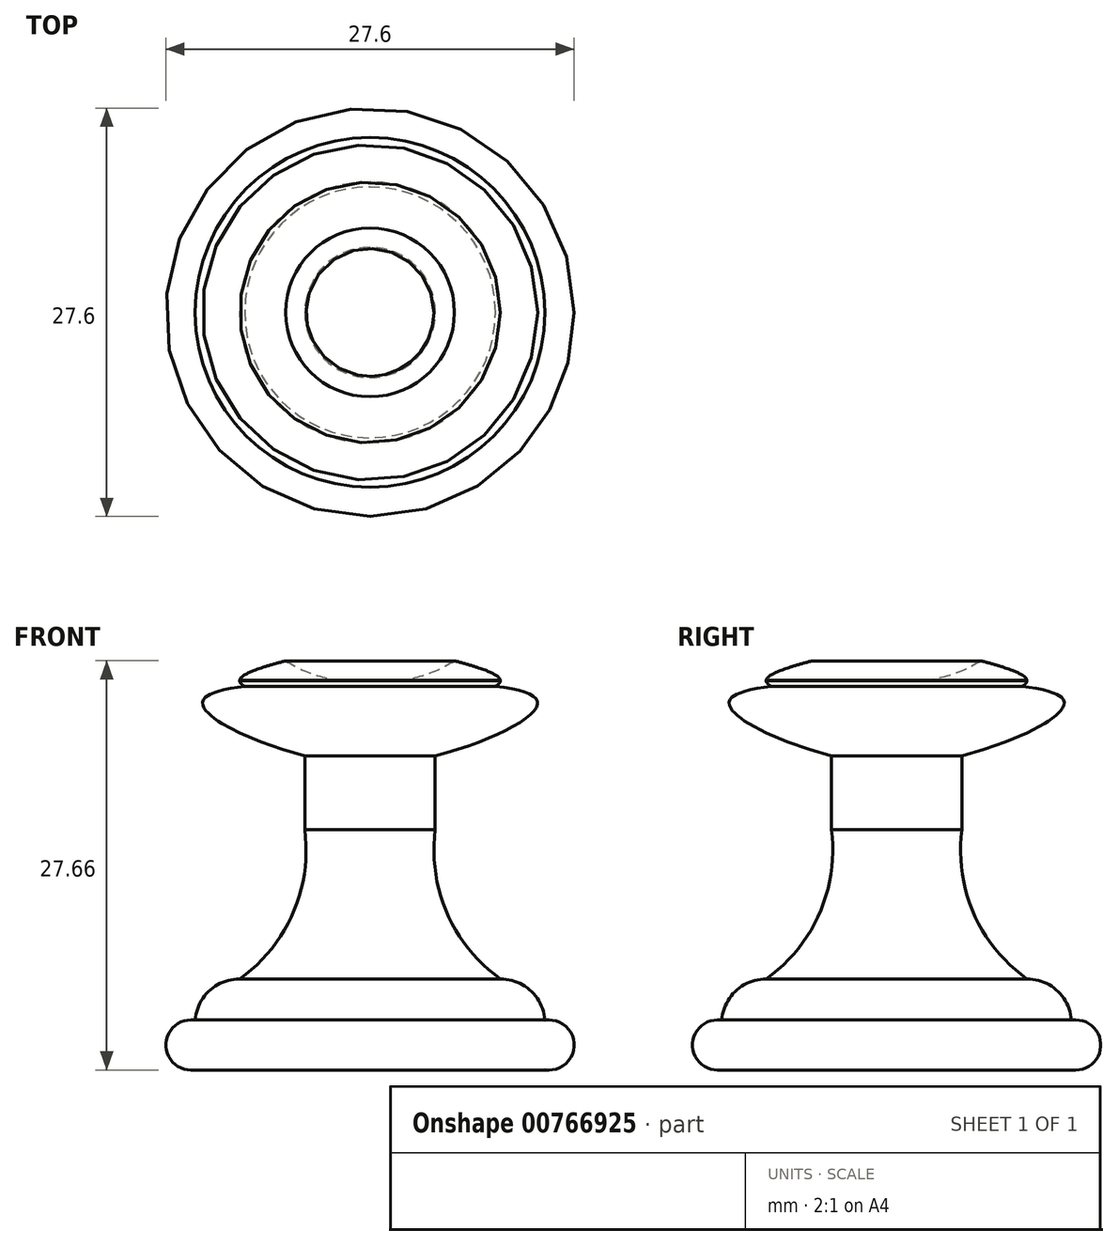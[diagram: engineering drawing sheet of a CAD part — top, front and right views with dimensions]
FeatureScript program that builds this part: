
annotation { "Feature Type Name" : "Feature", "Feature Type Description" : "" }
export const myFeature = defineFeature(function(context is Context, id is Id, definition is map)
    precondition{}
    {
        {
            var Q0;
            Q0=qCreatedBy(makeId("Front.planeOp"),FACE);
            var sketch = newSketch(context, id + "F0", { "sketchPlane" : qUnion([Q0])});
            skLineSegment(sketch, "E0.left", {"start": v(0, 2.22) * mm, "end": v(0, 4.66) * mm});
            skLineSegment(sketch, "E1", {"start": v(0, 4.66) * mm, "end": v(0, 8.36) * mm});
            skLineSegment(sketch, "E2", {"start": v(8.81, 8.36) * mm, "end": v(0, 8.36) * mm});
            skLineSegment(sketch, "E3", {"start": v(0, 8.36) * mm, "end": v(0, 28.5) * mm});
            skLineSegment(sketch, "E4", {"start": v(0, 28.5) * mm, "end": v(0, 38.78) * mm});
            skLineSegment(sketch, "E5", {"start": v(8.81, 28.5) * mm, "end": v(8.81, 28.52) * mm});
            skLineSegment(sketch, "E6", {"start": v(0, 28.5) * mm, "end": v(0, 18.43) * mm});
            skLineSegment(sketch, "E7", {"start": v(0, 38.78) * mm, "end": v(0, 46.36) * mm});
            skLineSegment(sketch, "E8", {"start": v(4.4, 23.44) * mm, "end": v(4.4, 18.43) * mm});
            skArc(sketch, "E9", {"start": v(4.4, 18.43) * mm, "mid": v(5.22, 12.78) * mm, "end": v(8.81, 8.36) * mm});
            skPoint(sketch, "E10.orphan", {"position": v(4.4, 8.36) * mm});
            skFitSpline(sketch, "E11", {"points": [v(4.4, 30.2) * mm, v(8.81, 28.5) * mm, v(0, 26.21) * mm], "startDerivative": vector(15.9, -4.06) * mm, "endDerivative": vector(-22.63, -3.9) * mm});
            skPoint(sketch, "E12.orphan", {"position": v(4.4, 28.5) * mm});
            skPoint(sketch, "E13.trimOffspring.end.orphan", {"position": v(8.81, 38.78) * mm});
            skPoint(sketch, "E14.2.internal.snap0", {"position": v(4.4, 22.72) * mm});
            skFitSpline(sketch, "E14", {"points": [v(0, 28.5) * mm, v(11.33, 27) * mm, v(0, 22.72) * mm, v(-17.97, 28.5) * mm], "startDerivative": vector(56.32, -0.98) * mm, "endDerivative": vector(-43.73, 24.03) * mm});
            skArc(sketch, "E15", {"start": v(0, 28.5) * mm, "mid": v(9.86, 37.43) * mm, "end": v(0, 46.36) * mm});
            skPoint(sketch, "E16.start.orphan", {"position": v(8.81, 4.66) * mm});
            skPoint(sketch, "E17.orphan", {"position": v(4.4, 27) * mm});
            skArc(sketch, "E18", {"start": v(3.4, 28.81) * mm, "mid": v(5.41, 28.82) * mm, "end": v(7.35, 29.38) * mm});
            skLineSegment(sketch, "E19", {"start": v(12.4, 5.56) * mm, "end": v(0, 5.56) * mm});
            skLineSegment(sketch, "E20", {"start": v(12.4, 2.22) * mm, "end": v(0, 2.22) * mm});
            skArc(sketch, "E21", {"start": v(11.82, 5.56) * mm, "mid": v(10.87, 7.55) * mm, "end": v(8.81, 8.36) * mm});
            skLineSegment(sketch, "E22", {"start": v(11.82, 5.56) * mm, "end": v(11.82, 2.22) * mm});
            skArc(sketch, "E23", {"start": v(11.82, 2.22) * mm, "mid": v(13.8, 3.89) * mm, "end": v(11.82, 5.56) * mm});
            skSolve(sketch);
        }
        {
            var Q0;
            Q0 = qSketchRegion(id + "F0", true);
            var Q1;
            Q1=sQuery(id+"F0.wireOp",EDGE,"E6");
            revolve(context, id + "F1", {"surfaceOperationType" : NewSurfaceOperationType.NEW, "entities" : qUnion([Q0]), "axis" : qUnion([Q1]), "revolveType" : RevolveType.FULL});
        }
    });
